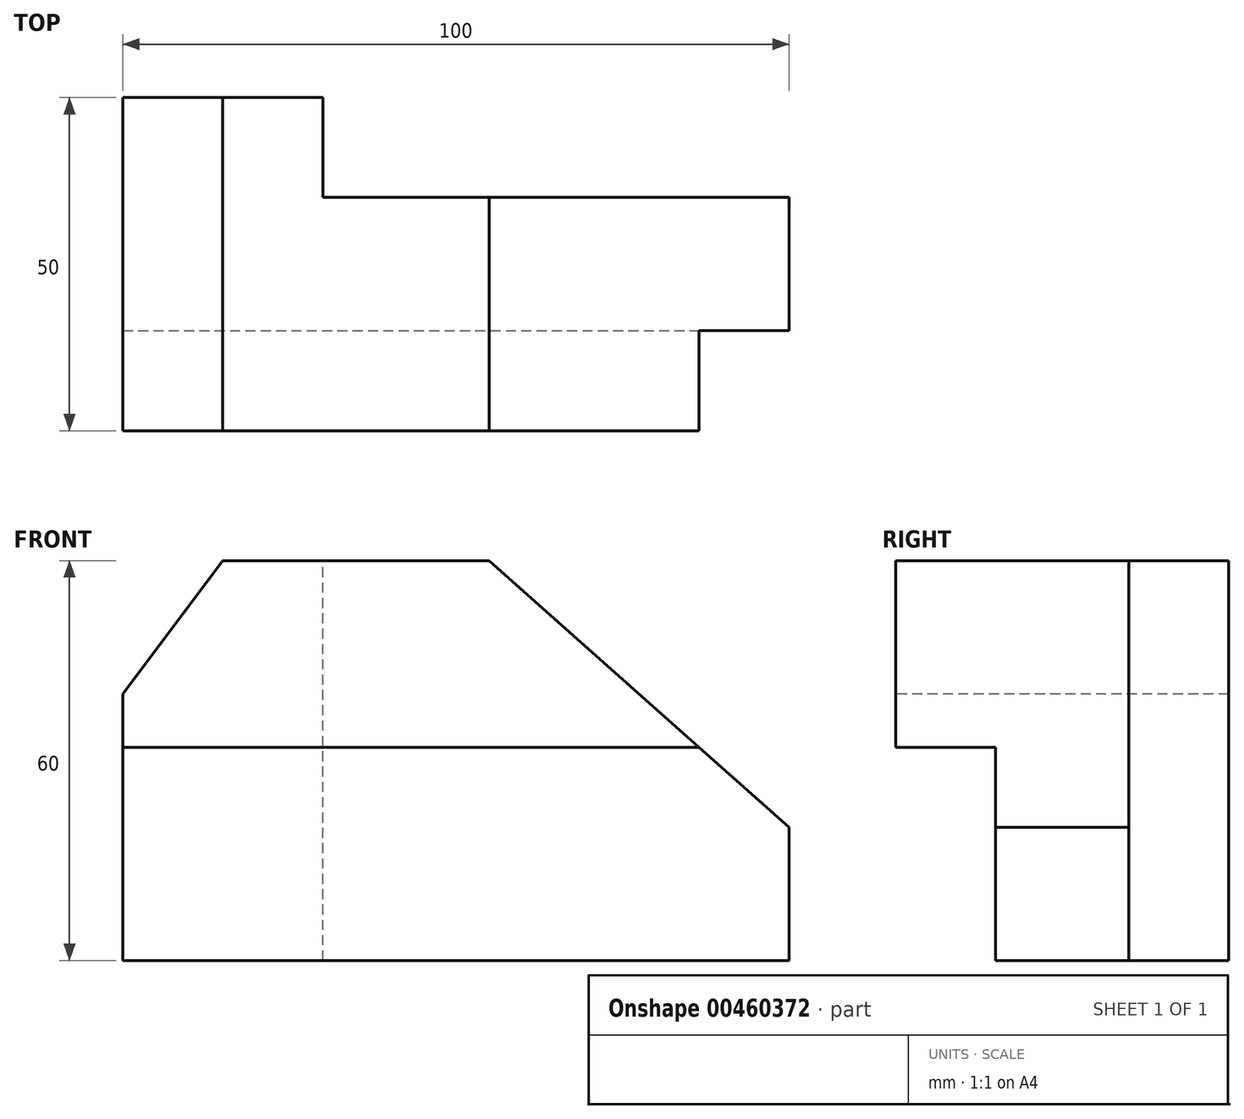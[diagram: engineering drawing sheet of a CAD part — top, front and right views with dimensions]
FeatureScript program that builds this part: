
annotation { "Feature Type Name" : "Feature", "Feature Type Description" : "" }
export const myFeature = defineFeature(function(context is Context, id is Id, definition is map)
    precondition{}
    {
        {
            var Q0;
            Q0=qCreatedBy(makeId("Front.planeOp"),FACE);
            var sketch = newSketch(context, id + "F0", { "sketchPlane" : qUnion([Q0])});
            skLineSegment(sketch, "E0.bottom", {"start": v(0, 0) * mm, "end": v(-100, 0) * mm});
            skLineSegment(sketch, "E0.top", {"start": v(0, 60) * mm, "end": v(-100, 60) * mm});
            skLineSegment(sketch, "E0.left", {"start": v(0, 0) * mm, "end": v(0, 60) * mm});
            skLineSegment(sketch, "E0.right", {"start": v(-100, 0) * mm, "end": v(-100, 60) * mm});
            skLineSegment(sketch, "E1", {"start": v(0, 60) * mm, "end": v(-45, 60) * mm});
            skLineSegment(sketch, "E2", {"start": v(0, 20) * mm, "end": v(0, 60) * mm});
            skSolve(sketch);
        }
        {
            var Q0;
            Q0=makeQuery(id+"F0.imprint","IMPRINT",FACE,{"disambiguationData":[TD([[makeQuery(id+"F0.imprint","IMPRINT",EDGE,{"derivedFrom":sQuery(id+"F0.wireOp",EDGE,"E0.bottom")}),-1.0]])]});
            extrude(context, id + "F1", {"entities" : qUnion([Q0]), "depth" : 50 * mm});
        }
        {
            var Q0;
            Q0=makeQuery(id+"F1.opExtrude","SWEPT_FACE",FACE,{"disambiguationData":[OSD([sQuery(id+"F0.wireOp",EDGE,"E0.left")])]});
            var sketch = newSketch(context, id + "F2", { "sketchPlane" : qUnion([Q0])});
            skLineSegment(sketch, "E3.bottom", {"start": v(-50, 0) * mm, "end": v(-35, 0) * mm});
            skLineSegment(sketch, "E3.top", {"start": v(-50, 32) * mm, "end": v(-35, 32) * mm});
            skLineSegment(sketch, "E3.left", {"start": v(-50, 0) * mm, "end": v(-50, 32) * mm});
            skLineSegment(sketch, "E3.right", {"start": v(-35, 0) * mm, "end": v(-35, 32) * mm});
            skSolve(sketch);
        }
        {
            var Q0;
            Q0=makeQuery(id+"F2.imprint","IMPRINT",FACE,{"disambiguationData":[TD([[makeQuery(id+"F2.imprint","IMPRINT",EDGE,{"derivedFrom":sQuery(id+"F2.wireOp",EDGE,"E3.bottom")}),1.0]])]});
            extrude(context, id + "F3", {"entities" : qUnion([Q0]), "operationType" : NewBodyOperationType.REMOVE, "endBound" : BoundingType.UP_TO_NEXT, "oppositeDirection" : true, "depth" : 25 * mm});
        }
        {
            var Q0;
            Q0=makeQuery(id+"F1.opExtrude","SWEPT_FACE",FACE,{"disambiguationData":[OSD([sQuery(id+"F0.wireOp",EDGE,"E0.top")])]});
            var sketch = newSketch(context, id + "F4", { "sketchPlane" : qUnion([Q0])});
            skLineSegment(sketch, "E4.bottom", {"start": v(0, 0) * mm, "end": v(-70, 0) * mm});
            skLineSegment(sketch, "E4.top", {"start": v(0, -15) * mm, "end": v(-70, -15) * mm});
            skLineSegment(sketch, "E4.left", {"start": v(0, 0) * mm, "end": v(0, -15) * mm});
            skLineSegment(sketch, "E4.right", {"start": v(-70, 0) * mm, "end": v(-70, -15) * mm});
            skSolve(sketch);
        }
        {
            var Q0;
            Q0=makeQuery(id+"F4.imprint","IMPRINT",FACE,{"disambiguationData":[TD([[makeQuery(id+"F4.imprint","IMPRINT",EDGE,{"derivedFrom":sQuery(id+"F4.wireOp",EDGE,"E4.bottom")}),1.0]])]});
            extrude(context, id + "F5", {"entities" : qUnion([Q0]), "operationType" : NewBodyOperationType.REMOVE, "endBound" : BoundingType.UP_TO_NEXT, "oppositeDirection" : true, "depth" : 25 * mm});
        }
        {
            var Q0;
            Q0=makeQuery(id+"F1.opExtrude","CAP_FACE",FACE,{"disambiguationData":[OSD([sQuery(id+"F0.wireOp",EDGE,"E0.bottom"),sQuery(id+"F0.wireOp",EDGE,"E0.top"),sQuery(id+"F0.wireOp",EDGE,"E0.left"),sQuery(id+"F0.wireOp",EDGE,"E0.right")])],"isStart":false});
            var sketch = newSketch(context, id + "F6", { "sketchPlane" : qUnion([Q0])});
            skLineSegment(sketch, "E5", {"start": v(-100, 60) * mm, "end": v(-85, 60) * mm});
            skLineSegment(sketch, "E6", {"start": v(-85, 60) * mm, "end": v(-100, 40) * mm});
            skLineSegment(sketch, "E7", {"start": v(-100, 40) * mm, "end": v(-100, 60) * mm});
            skSolve(sketch);
        }
        {
            var Q0;
            Q0=makeQuery(id+"F6.imprint","IMPRINT",FACE,{"disambiguationData":[TD([[makeQuery(id+"F6.imprint","IMPRINT",EDGE,{"derivedFrom":sQuery(id+"F6.wireOp",EDGE,"E5")}),1.0]])]});
            extrude(context, id + "F7", {"entities" : qUnion([Q0]), "operationType" : NewBodyOperationType.REMOVE, "endBound" : BoundingType.UP_TO_NEXT, "oppositeDirection" : true, "depth" : 25 * mm});
        }
        {
            var Q0;
            Q0=makeQuery(id+"F1.opExtrude","CAP_FACE",FACE,{"disambiguationData":[OSD([sQuery(id+"F0.wireOp",EDGE,"E0.bottom"),sQuery(id+"F0.wireOp",EDGE,"E0.top"),sQuery(id+"F0.wireOp",EDGE,"E0.left"),sQuery(id+"F0.wireOp",EDGE,"E0.right"),sQuery(id+"F0.wireOp",EDGE,"E1"),sQuery(id+"F0.wireOp",EDGE,"E2")])],"isStart":false});
            var sketch = newSketch(context, id + "F8", { "sketchPlane" : qUnion([Q0])});
            skLineSegment(sketch, "E8", {"start": v(0, 60) * mm, "end": v(-45, 60) * mm});
            skLineSegment(sketch, "E9", {"start": v(-45, 60) * mm, "end": v(0, 20) * mm});
            skLineSegment(sketch, "E10", {"start": v(0, 20) * mm, "end": v(0, 60) * mm});
            skSolve(sketch);
        }
        {
            var Q0;
            {var subQ0=sQuery(id+"F8.wireOp",EDGE,"E8");Q0=makeQuery(id+"F8.imprint","IMPRINT",FACE,{"disambiguationData":[TD([[makeQuery(id+"F8.imprint","IMPRINT",EDGE,{"derivedFrom":subQ0}),1.0]])]});}
            var Q1;
            {var subQ0=sQuery(id+"F8.wireOp",EDGE,"E10");var subQ1=sQuery(id+"F8.wireOp",EDGE,"E9");var subQ2=makeQuery(id+"F8.imprint","INTERSECT",VERTEX,{"derivedFrom":[subQ1,subQ0]});Q1=makeQuery(id+"F8.imprint","IMPRINT",FACE,{"disambiguationData":[TD([[makeQuery(id+"F8.imprint","IMPRINT",EDGE,{"disambiguationData":[TD([[subQ2,1.0]])],"derivedFrom":subQ1}),1.0]])]});}
            extrude(context, id + "F9", {"entities" : qUnion([Q0, Q1]), "operationType" : NewBodyOperationType.REMOVE, "endBound" : BoundingType.UP_TO_NEXT, "oppositeDirection" : true, "depth" : 25 * mm});
        }
    });
